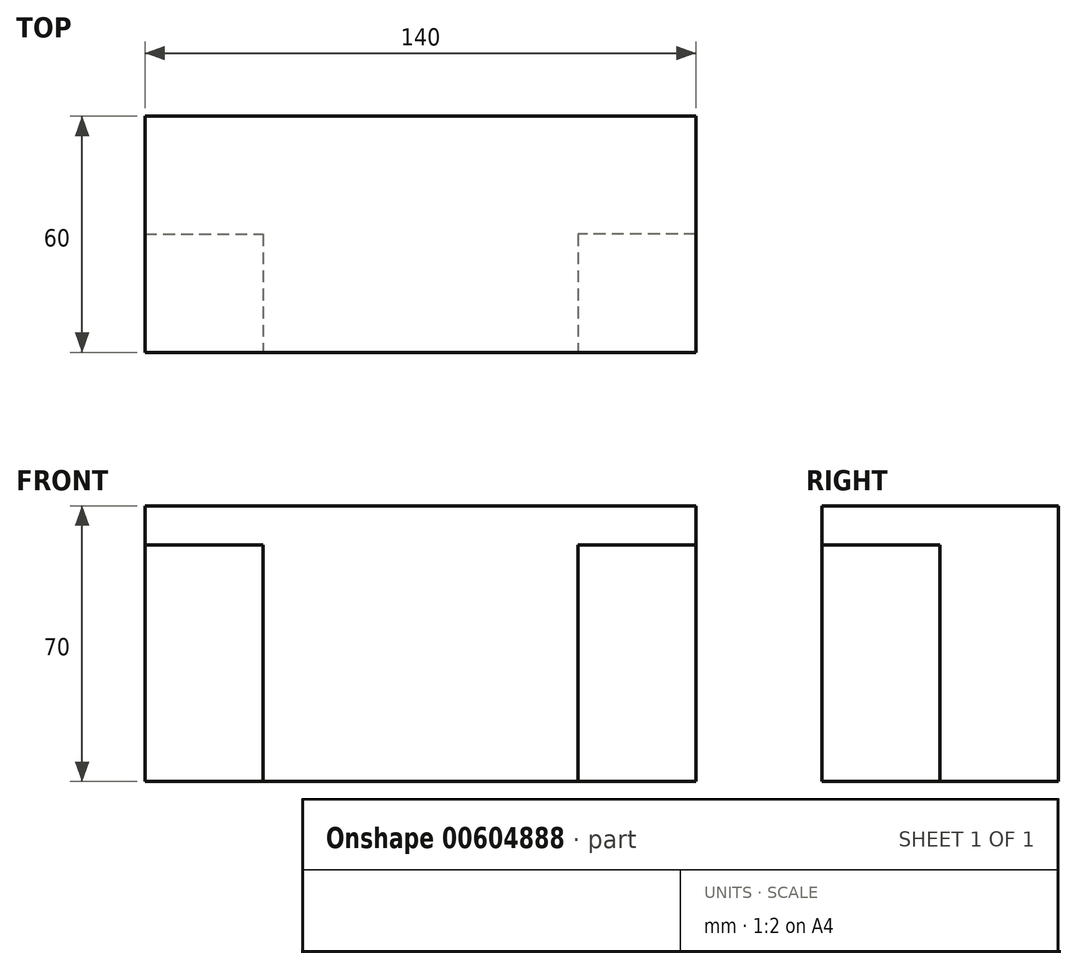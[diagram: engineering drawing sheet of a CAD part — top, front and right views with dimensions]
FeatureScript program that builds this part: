
annotation { "Feature Type Name" : "Feature", "Feature Type Description" : "" }
export const myFeature = defineFeature(function(context is Context, id is Id, definition is map)
    precondition{}
    {
        {
            var Q0;
            Q0=qCreatedBy(makeId("Front.planeOp"),FACE);
            var sketch = newSketch(context, id + "F0", { "sketchPlane" : qUnion([Q0])});
            skLineSegment(sketch, "E0", {"start": v(-62.64, 47.95) * mm, "end": v(77.36, 47.95) * mm});
            skLineSegment(sketch, "E1", {"start": v(77.36, 47.95) * mm, "end": v(77.36, -22.05) * mm});
            skLineSegment(sketch, "E2", {"start": v(77.36, -22.05) * mm, "end": v(-62.64, -22.05) * mm});
            skLineSegment(sketch, "E3", {"start": v(-62.64, -22.05) * mm, "end": v(-62.64, 47.95) * mm});
            skSolve(sketch);
        }
        {
            var Q0;
            Q0=makeQuery(id+"F0.imprint","IMPRINT",FACE,{"disambiguationData":[TD([[makeQuery(id+"F0.imprint","IMPRINT",EDGE,{"derivedFrom":sQuery(id+"F0.wireOp",EDGE,"E0")}),-1.0]])]});
            extrude(context, id + "F1", {"entities" : qUnion([Q0]), "depth" : 60 * mm, "offsetDistance" : 25 * mm});
        }
        {
            var Q0;
            Q0=makeQuery(id+"F1.opExtrude","SWEPT_FACE",FACE,{"disambiguationData":[OSD([sQuery(id+"F0.wireOp",EDGE,"E2")])]});
            var sketch = newSketch(context, id + "F2", { "sketchPlane" : qUnion([Q0])});
            skLineSegment(sketch, "E4", {"start": v(-62.64, 30) * mm, "end": v(-32.64, 30) * mm});
            skLineSegment(sketch, "E5", {"start": v(-32.64, 30) * mm, "end": v(-32.64, 60) * mm});
            skLineSegment(sketch, "E6", {"start": v(-32.64, 60) * mm, "end": v(-62.64, 60) * mm});
            skLineSegment(sketch, "E7", {"start": v(-62.64, 60) * mm, "end": v(-62.64, 30) * mm});
            skSolve(sketch);
        }
        {
            var Q0;
            Q0=makeQuery(id+"F2.imprint","IMPRINT",FACE,{"disambiguationData":[TD([[makeQuery(id+"F2.imprint","IMPRINT",EDGE,{"derivedFrom":sQuery(id+"F2.wireOp",EDGE,"E4")}),1.0]])]});
            extrude(context, id + "F3", {"entities" : qUnion([Q0]), "operationType" : NewBodyOperationType.REMOVE, "oppositeDirection" : true, "depth" : 60 * mm, "offsetDistance" : 25 * mm});
        }
        {
            var Q0;
            Q0=makeQuery(id+"F1.opExtrude","SWEPT_FACE",FACE,{"disambiguationData":[OSD([sQuery(id+"F0.wireOp",EDGE,"E2")])]});
            var sketch = newSketch(context, id + "F4", { "sketchPlane" : qUnion([Q0])});
            skLineSegment(sketch, "E8", {"start": v(77.36, 30) * mm, "end": v(47.36, 30) * mm});
            skPoint(sketch, "E8.endSnap0", {"position": v(77.36, 30) * mm});
            skLineSegment(sketch, "E9", {"start": v(47.36, 30) * mm, "end": v(47.36, 60) * mm});
            skLineSegment(sketch, "E10", {"start": v(47.36, 60) * mm, "end": v(77.36, 60) * mm});
            skLineSegment(sketch, "E11", {"start": v(77.36, 60) * mm, "end": v(77.36, 30) * mm});
            skSolve(sketch);
        }
        {
            var Q0;
            Q0=makeQuery(id+"F4.imprint","IMPRINT",FACE,{"disambiguationData":[TD([[makeQuery(id+"F4.imprint","IMPRINT",EDGE,{"derivedFrom":sQuery(id+"F4.wireOp",EDGE,"E8")}),-1.0]])]});
            extrude(context, id + "F5", {"entities" : qUnion([Q0]), "operationType" : NewBodyOperationType.REMOVE, "oppositeDirection" : true, "depth" : 60 * mm, "offsetDistance" : 25 * mm});
        }
    });
